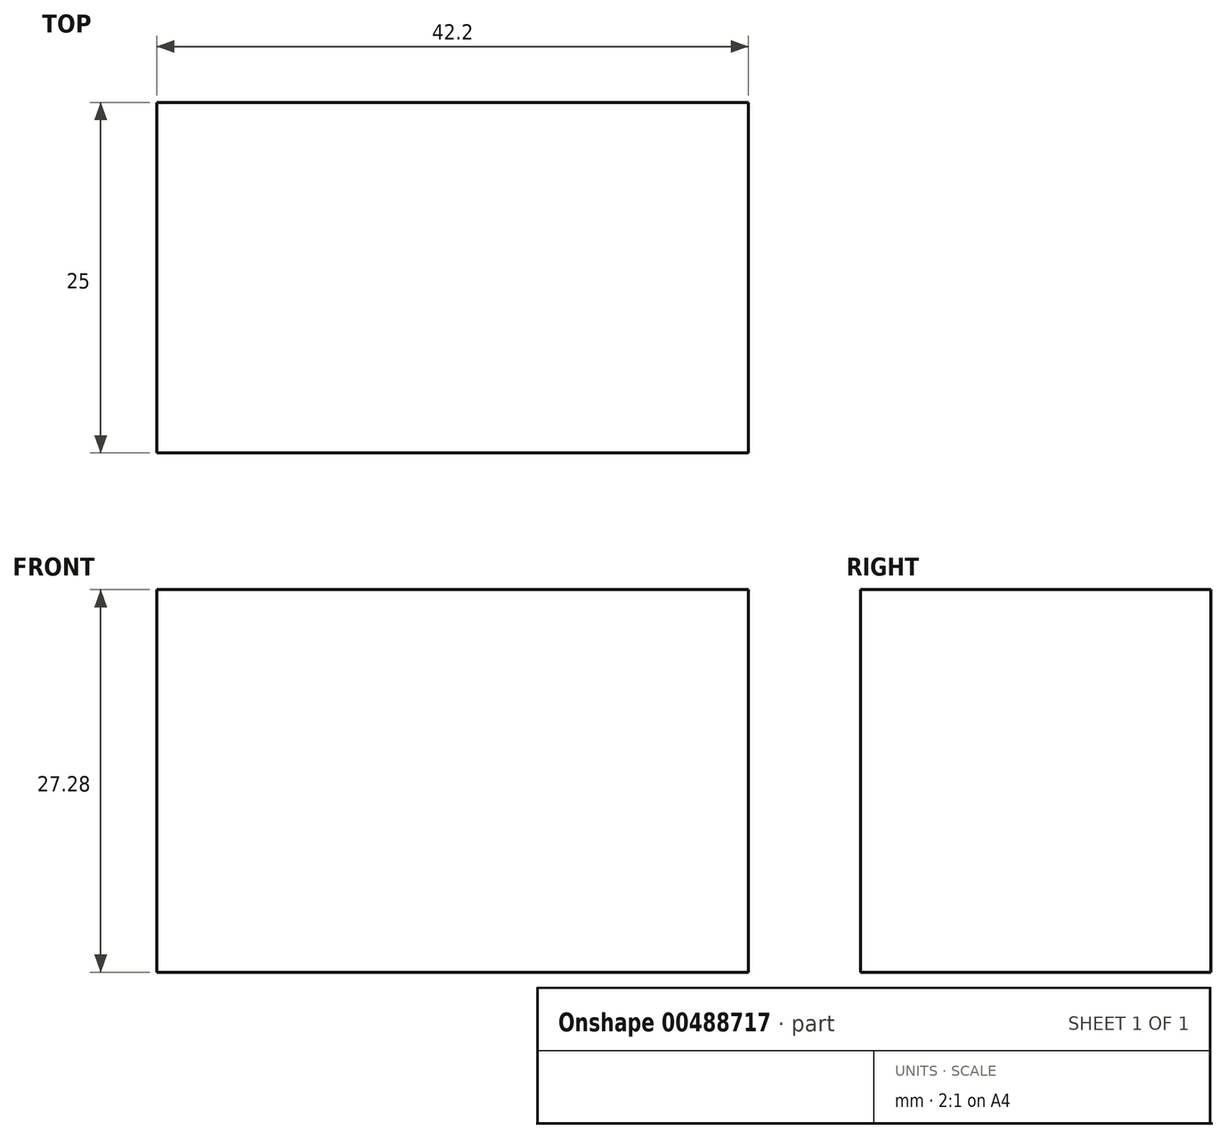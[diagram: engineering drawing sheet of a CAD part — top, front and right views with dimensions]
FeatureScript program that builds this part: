
annotation { "Feature Type Name" : "Feature", "Feature Type Description" : "" }
export const myFeature = defineFeature(function(context is Context, id is Id, definition is map)
    precondition{}
    {
        {
            var Q0;
            Q0=qCreatedBy(makeId("Front.planeOp"),FACE);
            var sketch = newSketch(context, id + "F0", { "sketchPlane" : qUnion([Q0])});
            skLineSegment(sketch, "E0.bottom", {"start": v(-124.37, 37.91) * mm, "end": v(-82.17, 37.91) * mm});
            skLineSegment(sketch, "E0.top", {"start": v(-124.37, 10.63) * mm, "end": v(-82.17, 10.63) * mm});
            skLineSegment(sketch, "E0.left", {"start": v(-124.37, 37.91) * mm, "end": v(-124.37, 10.63) * mm});
            skLineSegment(sketch, "E0.right", {"start": v(-82.17, 37.91) * mm, "end": v(-82.17, 10.63) * mm});
            skSolve(sketch);
        }
        {
            var Q0;
            Q0 = qSketchRegion(id + "F0", true);
            extrude(context, id + "F1", {"entities" : qUnion([Q0]), "depth" : 25 * mm});
        }
    });
